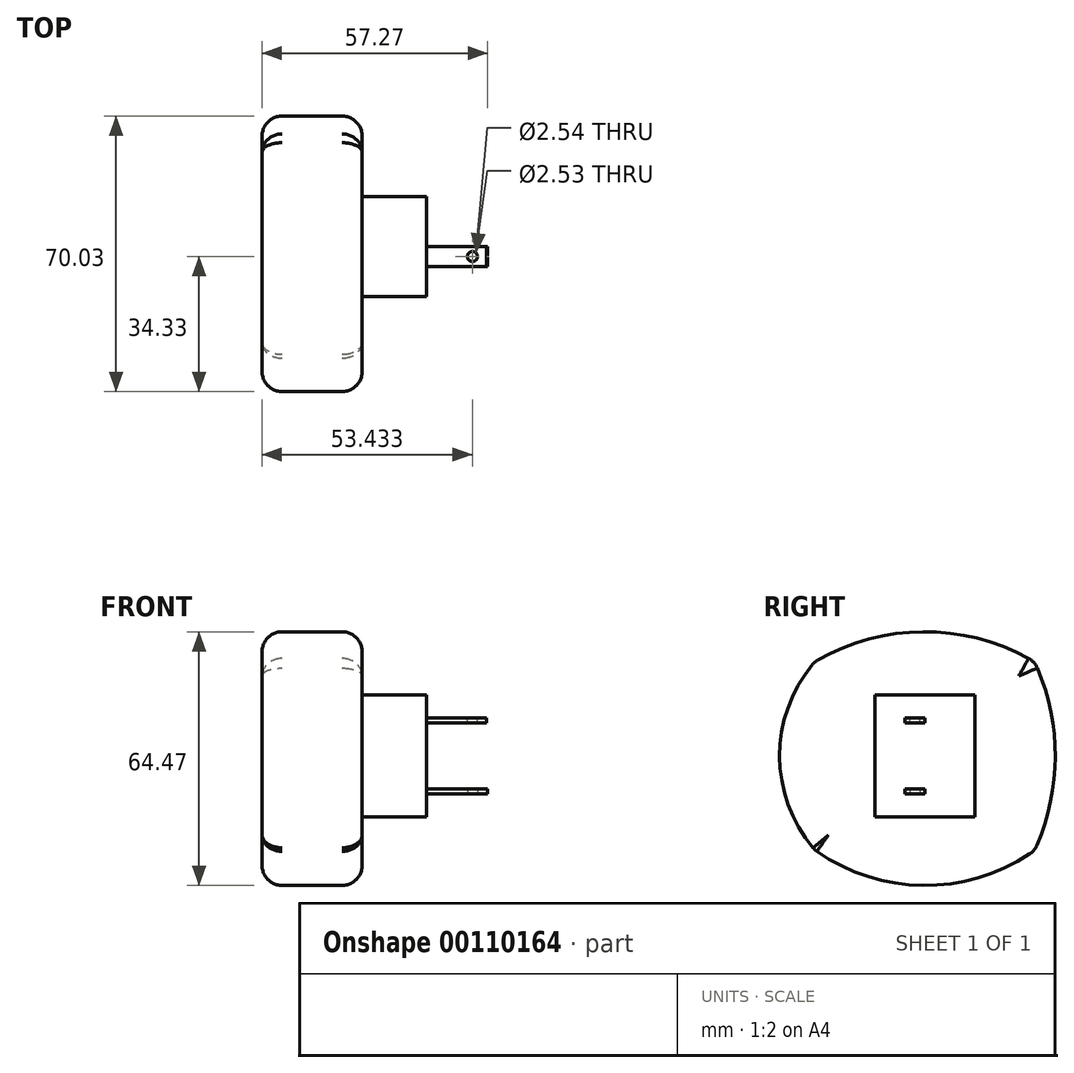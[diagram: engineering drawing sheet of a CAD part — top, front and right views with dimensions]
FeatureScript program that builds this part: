
annotation { "Feature Type Name" : "Feature", "Feature Type Description" : "" }
export const myFeature = defineFeature(function(context is Context, id is Id, definition is map)
    precondition{}
    {
        {
            var Q0;
            Q0=qCreatedBy(makeId("Front.planeOp"),FACE);
            var sketch = newSketch(context, id + "F0", { "sketchPlane" : qUnion([Q0])});
            skLineSegment(sketch, "E0.bottom", {"start": v(-68.62, 57.69) * mm, "end": v(-52.27, 57.69) * mm});
            skLineSegment(sketch, "E0.top", {"start": v(-68.62, 26.65) * mm, "end": v(-52.27, 26.65) * mm});
            skLineSegment(sketch, "E0.left", {"start": v(-68.62, 57.69) * mm, "end": v(-68.62, 26.65) * mm});
            skLineSegment(sketch, "E0.right", {"start": v(-52.27, 57.69) * mm, "end": v(-52.27, 26.65) * mm});
            skLineSegment(sketch, "E1.bottom", {"start": v(-52.27, 51.85) * mm, "end": v(-37.03, 51.85) * mm});
            skLineSegment(sketch, "E1.top", {"start": v(-52.27, 50.58) * mm, "end": v(-37.03, 50.58) * mm});
            skLineSegment(sketch, "E1.left", {"start": v(-52.27, 51.85) * mm, "end": v(-52.27, 50.58) * mm});
            skLineSegment(sketch, "E1.right", {"start": v(-37.03, 51.85) * mm, "end": v(-37.03, 50.58) * mm});
            skLineSegment(sketch, "E2.bottom", {"start": v(-52.27, 33.77) * mm, "end": v(-36.75, 33.77) * mm});
            skLineSegment(sketch, "E2.top", {"start": v(-52.27, 32.5) * mm, "end": v(-36.75, 32.5) * mm});
            skLineSegment(sketch, "E2.left", {"start": v(-52.27, 33.77) * mm, "end": v(-52.27, 32.5) * mm});
            skLineSegment(sketch, "E2.right", {"start": v(-36.75, 33.77) * mm, "end": v(-36.75, 32.5) * mm});
            skSolve(sketch);
        }
        {
            var Q0;
            Q0=makeQuery(id+"F0.imprint","IMPRINT",FACE,{"disambiguationData":[TD([[makeQuery(id+"F0.imprint","IMPRINT",EDGE,{"derivedFrom":sQuery(id+"F0.wireOp",EDGE,"E1.bottom")}),-1.0]])]});
            var Q1;
            Q1=makeQuery(id+"F0.imprint","IMPRINT",FACE,{"disambiguationData":[TD([[makeQuery(id+"F0.imprint","IMPRINT",EDGE,{"derivedFrom":sQuery(id+"F0.wireOp",EDGE,"E2.bottom")}),-1.0]])]});
            extrude(context, id + "F1", {"entities" : qUnion([Q0, Q1]), "depth" : 5.08 * mm});
        }
        {
            var Q0;
            {var subQ1=sQuery(id+"F0.wireOp",EDGE,"E0.bottom");Q0=makeQuery(id+"F0.imprint","IMPRINT",FACE,{"disambiguationData":[TD([[makeQuery(id+"F0.imprint","IMPRINT",EDGE,{"derivedFrom":subQ1}),-1.0]])]});}
            extrude(context, id + "F2", {"entities" : qUnion([Q0]), "depth" : 12.7 * mm, "hasSecondDirection" : true, "secondDirectionOppositeDirection" : true, "secondDirectionDepth" : 12.7 * mm});
        }
        {
            var Q0;
            Q0=makeQuery(id+"F1.opExtrude","SWEPT_FACE",FACE,{"disambiguationData":[OSD([sQuery(id+"F0.wireOp",EDGE,"E1.bottom")])]});
            var sketch = newSketch(context, id + "F3", { "sketchPlane" : qUnion([Q0])});
            skCircle(sketch, "E3", {"center": v(-40.59, -2.54) * mm, "radius": 1.27 * mm});
            skPoint(sketch, "E3.centerSnap0", {"position": v(-37.03, -2.54) * mm});
            skSolve(sketch);
        }
        {
            var Q0;
            Q0=makeQuery(id+"F3.imprint","IMPRINT",FACE,{"disambiguationData":[TD([[makeQuery(id+"F3.imprint","IMPRINT",EDGE,{"derivedFrom":sQuery(id+"F3.wireOp",EDGE,"E3")}),1.0]])]});
            extrude(context, id + "F4", {"entities" : qUnion([Q0]), "operationType" : NewBodyOperationType.REMOVE, "oppositeDirection" : true, "depth" : 5.08 * mm});
        }
        {
            var Q0;
            Q0=makeQuery(id+"F1.opExtrude","SWEPT_FACE",FACE,{"disambiguationData":[OSD([sQuery(id+"F0.wireOp",EDGE,"E2.top")])]});
            var sketch = newSketch(context, id + "F5", { "sketchPlane" : qUnion([Q0])});
            skCircle(sketch, "E4", {"center": v(-40.59, 2.54) * mm, "radius": 1.27 * mm});
            skSolve(sketch);
        }
        {
            var Q0;
            Q0=makeQuery(id+"F5.imprint","IMPRINT",FACE,{"disambiguationData":[TD([[makeQuery(id+"F5.imprint","IMPRINT",EDGE,{"derivedFrom":sQuery(id+"F5.wireOp",EDGE,"E4")}),1.0]])]});
            extrude(context, id + "F6", {"entities" : qUnion([Q0]), "operationType" : NewBodyOperationType.REMOVE, "oppositeDirection" : true, "depth" : 5.08 * mm});
        }
        {
            var Q0;
            Q0=makeQuery(id+"F2.opExtrude","SWEPT_FACE",FACE,{"disambiguationData":[OSD([sQuery(id+"F0.wireOp",EDGE,"E0.left")])]});
            var sketch = newSketch(context, id + "F7", { "sketchPlane" : qUnion([Q0])});
            skLineSegment(sketch, "E5.bottom", {"start": v(27.94, 65.98) * mm, "end": v(-27.94, 65.98) * mm});
            skLineSegment(sketch, "E5.top", {"start": v(27.94, 18.15) * mm, "end": v(-27.94, 18.15) * mm});
            skLineSegment(sketch, "E5.left", {"start": v(27.94, 65.98) * mm, "end": v(27.94, 18.15) * mm});
            skLineSegment(sketch, "E5.right", {"start": v(-27.94, 65.98) * mm, "end": v(-27.94, 18.15) * mm});
            skPoint(sketch, "E5.middle", {"position": v(0, 42.07) * mm});
            skSolve(sketch);
        }
        {
            var Q0;
            {var subQ0=sQuery(id+"F0.wireOp",EDGE,"E0.left");Q0=makeQuery(id+"F7.imprint","IMPRINT",FACE,{"disambiguationData":[TD([[makeQuery(id+"F7.imprint","IMPRINT",EDGE,{"derivedFrom":makeQuery(id+"F2.opExtrude","CAP_EDGE",EDGE,{"disambiguationData":[OSD([subQ0])],"isStart":true})}),1.0]])]});}
            var sketch = newSketch(context, id + "F8", { "sketchPlane" : qUnion([Q0])});
            skArc(sketch, "E6", {"start": v(-27.91, 66.1) * mm, "mid": v(-33.16, 42.11) * mm, "end": v(-27.91, 18.12) * mm});
            skArc(sketch, "E7", {"start": v(27.91, 66.1) * mm, "mid": v(0, 73.73) * mm, "end": v(-27.91, 66.1) * mm});
            skArc(sketch, "E8", {"start": v(27.91, 18.31) * mm, "mid": v(36.87, 42.2) * mm, "end": v(27.91, 66.1) * mm});
            skArc(sketch, "E9", {"start": v(-27.91, 18.12) * mm, "mid": v(0.03, 9.26) * mm, "end": v(27.91, 18.31) * mm});
            skSolve(sketch);
        }
        {
            var Q0;
            {var subQ0=sQuery(id+"F0.wireOp",EDGE,"E0.left");Q0=makeQuery(id+"F8.imprint","IMPRINT",FACE,{"disambiguationData":[TD([[makeQuery(id+"F8.imprint","IMPRINT",EDGE,{"derivedFrom":makeQuery(id+"F7.imprint","IMPRINT",EDGE,{"derivedFrom":makeQuery(id+"F2.opExtrude","CAP_EDGE",EDGE,{"disambiguationData":[OSD([subQ0])],"isStart":true})})}),1.0]])]});}
            var Q1;
            Q1=makeQuery(id+"F8.imprint","IMPRINT",FACE,{"disambiguationData":[TD([[makeQuery(id+"F8.imprint","IMPRINT",EDGE,{"derivedFrom":sQuery(id+"F8.wireOp",EDGE,"E6")}),1.0]])]});
            extrude(context, id + "F9", {"entities" : qUnion([Q0, Q1]), "operationType" : NewBodyOperationType.ADD, "depth" : 25.4 * mm});
        }
        {
            var Q0;
            Q0=makeQuery(id+"F9.opExtrude","SWEPT_FACE",FACE,{"disambiguationData":[OSD([sQuery(id+"F8.wireOp",EDGE,"E9")])]});
            var Q1;
            Q1=makeQuery(id+"F9.opExtrude","SWEPT_FACE",FACE,{"disambiguationData":[OSD([sQuery(id+"F8.wireOp",EDGE,"E6")])]});
            fillet(context, id + "F10", {"entities" : qUnion([Q0, Q1]), "radius" : 5.08 * mm, "tangentPropagation" : true, "allowEdgeOverflow" : false});
        }
        {
            var Q0;
            Q0=makeQuery(id+"F9.opExtrude","SWEPT_FACE",FACE,{"disambiguationData":[OSD([sQuery(id+"F8.wireOp",EDGE,"E7")])]});
            var Q1;
            Q1=makeQuery(id+"F9.opExtrude","SWEPT_FACE",FACE,{"disambiguationData":[OSD([sQuery(id+"F8.wireOp",EDGE,"E8")])]});
            fillet(context, id + "F11", {"entities" : qUnion([Q0, Q1]), "radius" : 5.08 * mm, "tangentPropagation" : true, "allowEdgeOverflow" : false});
        }
    });
